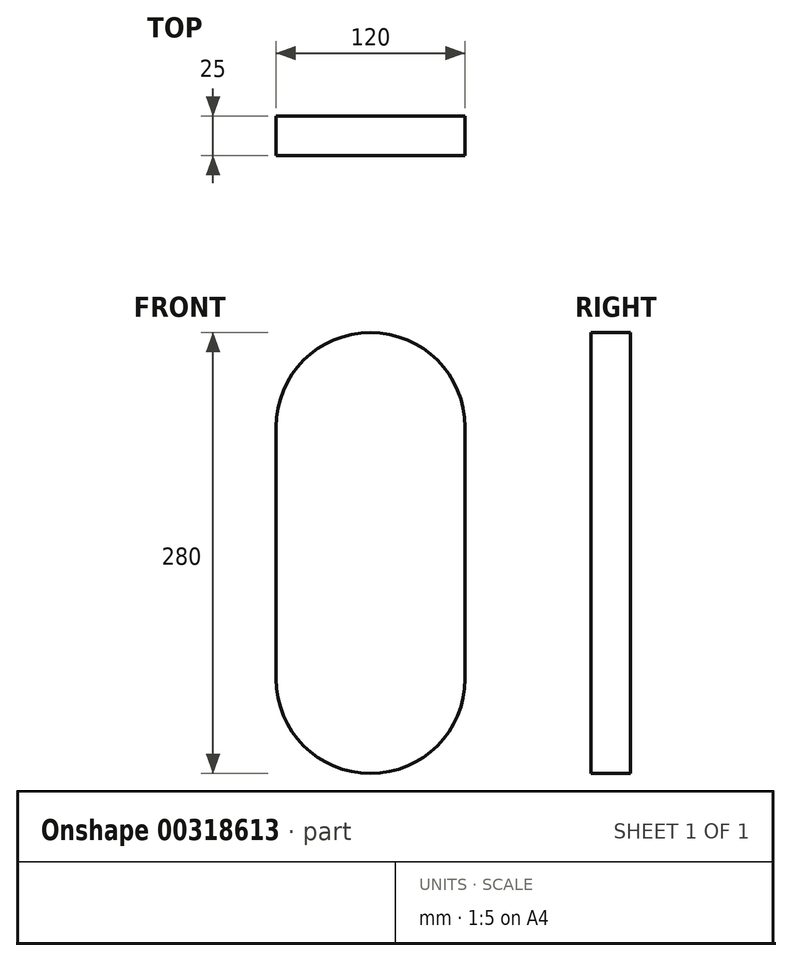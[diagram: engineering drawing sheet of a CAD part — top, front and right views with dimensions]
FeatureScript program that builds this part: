
annotation { "Feature Type Name" : "Feature", "Feature Type Description" : "" }
export const myFeature = defineFeature(function(context is Context, id is Id, definition is map)
    precondition{}
    {
        {
            var Q0;
            Q0=qCreatedBy(makeId("Front.planeOp"),FACE);
            var sketch = newSketch(context, id + "F0", { "sketchPlane" : qUnion([Q0])});
            skLineSegment(sketch, "E0.rect.bottom", {"start": v(60, -80) * mm, "end": v(-60, -80) * mm, "construction": true});
            skLineSegment(sketch, "E0.rect.top", {"start": v(60, 80) * mm, "end": v(-60, 80) * mm, "construction": true});
            skLineSegment(sketch, "E0.rect.left", {"start": v(60, -80) * mm, "end": v(60, 80) * mm});
            skLineSegment(sketch, "E0.rect.right", {"start": v(-60, -80) * mm, "end": v(-60, 80) * mm});
            skPoint(sketch, "E0.rect.middle", {"position": v(0, 0) * mm});
            skArc(sketch, "E1", {"start": v(60, 80) * mm, "mid": v(0, 140) * mm, "end": v(-60, 80) * mm});
            skArc(sketch, "E2", {"start": v(-60, -80) * mm, "mid": v(0, -140) * mm, "end": v(60, -80) * mm});
            skSolve(sketch);
        }
        {
            var Q0;
            Q0=makeQuery(id+"F0.imprint","IMPRINT",FACE,{"disambiguationData":[TD([[makeQuery(id+"F0.imprint","IMPRINT",EDGE,{"derivedFrom":sQuery(id+"F0.wireOp",EDGE,"E0.rect.left")}),1.0]])]});
            extrude(context, id + "F1", {"entities" : qUnion([Q0]), "depth" : 10 * mm});
        }
        {
            var Q0;
            Q0=makeQuery(id+"F0.imprint","IMPRINT",FACE,{"disambiguationData":[TD([[makeQuery(id+"F0.imprint","IMPRINT",EDGE,{"derivedFrom":sQuery(id+"F0.wireOp",EDGE,"E0.rect.left")}),1.0]])]});
            extrude(context, id + "F2", {"entities" : qUnion([Q0]), "operationType" : NewBodyOperationType.ADD, "depth" : 25 * mm});
        }
    });
